# Revit family: Lighting_Pendants_Nordlux_Nexus_2.0_Small
name_source: partatom
category: Lighting Fixtures
revit_build: Autodesk Revit 2017 (Build: 20190508_0315(x64)
units: mm (PartAtom-declared; Revit-internal decimal feet)

## family parameters
Always vertical = Yes
Cut with Voids When Loaded = No
Host = Ceiling
Light Source = Yes
OmniClass Number = 23.80.70.11
OmniClass Title = Luminaries for Internal Lighting
Part Type = Normal
Room Calculation Point = No
Round Connector Dimension = Use Diameter
Shared = No

## types (2) — shared parameters
AssetType = Fixed
BIMObjectName = Lighting_Pendants_Nordlux_Nexus_2.0_Small
Brand = Nordlux
Category = Indoor lighting
Collection = Nexus 2.0
Color Filter = 16777215
ColourIndexRA = 80
ConvergoRefNr = 0143-1909-0009-DK
Description = NEXUS is an exciting series that epitomises Nordic cool. The details tell the story of an elegantly designed light, for example, the pendant’s invisible transition between shade and cord.
Designer = Bonnelycke MDD
Dimmer = Dimmable
Dimming Lamp Color Temperature Shift = <None>
DurationUnit = Hours
Emit Shape Visible in Rendering = No
Emit from Circle Diameter = 50 mm  [stored 0.164042 ft]
EnergyClass = A++ - A
ExpectedLife = 25000
Features = Textile cable 250cm. Cable can not be replaced.
Finish = Satin soft, matt surface. Primary material metal, secondary material plastic, textile cable
HasProtectiveEarth = No
IP_Code = IP20
IfcExportAs = IfcLightFixtureType
IfcExportType = NOTDEFINED
InsulationStandardClass = Class 2 (Double isolated)
LensMaterial = Glass
LightFixtureMountingType = Suspended
LightFixturePlacingType = Ceilling
LightSource = Incl. 3W LED SMD
Manufacturer = Nordlux
ManufacturerName = Nordlux
ManufacturerURL = https://www.nordlux.com
Material = Metal, plastic & textile
NBSDescription = General purpose luminaires
NBSReference = 90-60-50/405
Name = Nordlux_Nexus_2.0_Small
NominalCurrent = 0 A
NominalDiameter = 120 mm  [stored 0.393701 ft]
NominalFrequencyRange = 50 Hz
NominalLength = 120 mm  [stored 0.393701 ft]
NominalRadius = 60 mm  [stored 0.19685 ft]
NominalVoltage = 230 V
NominalVoltageCalc = 0 V
NominalWidth = 120 mm  [stored 0.393701 ft]
NumberOfPoles = 1
PhaseAngle = 0.00°
Photometric Web File = 7725 Nexus 10 Pendel.ies
Product data url = https://www.bimobject.com
ProductDatasheet = http://pim.skypim.com
Revision = 1
Shape = Sculptured
Size = Shade: 100x100x150 mm / Canopy: 120x120x90 mm
Socket = GU10
Tilt Angle = 90.00°
TotalWattage = 6 W
URL = https://www.nordlux.com
Uniclass2 = Pr_70_70_49_86
Uniclass2015Description = Pendant  luminaires
Uniclass2015Reference = Pr_70_70_48_62
UsageCurrent = 0 A
Version = 2
VersionDate = 01/07/2020
WarrantyDurationUnit = Hours
zero-valued in all types: DefaultElevation, ElectricalDeviceNominalPower, MaintenanceFactor, NumberOfSources

## per-type parameters (varying)
| type | ArticleNumber | Color | EANNumber | LightFixtureMainMaterial | LightFixtureSecondaryMaterial | ModelReference |
| Nexus 2.0 Pendant Small - white | 2020563001 | White RAL7047 | 5704924002328 | White | White cable | 2020563001 |
| Nexus 2.0 Pendant Small - black | 2020563003 | Black RAL9005 | 5704924002335 | Black | Black cable | 2020563003 |

note: column(s) folded — value = type name in every type: Model

note: [stored X ft] marks values corroborated as IEEE doubles in the binary element streams (Revit-internal decimal feet)

## geometry (parser evidence)
native form markers: Sweep x6
no freeform markers — native parametric forms only
